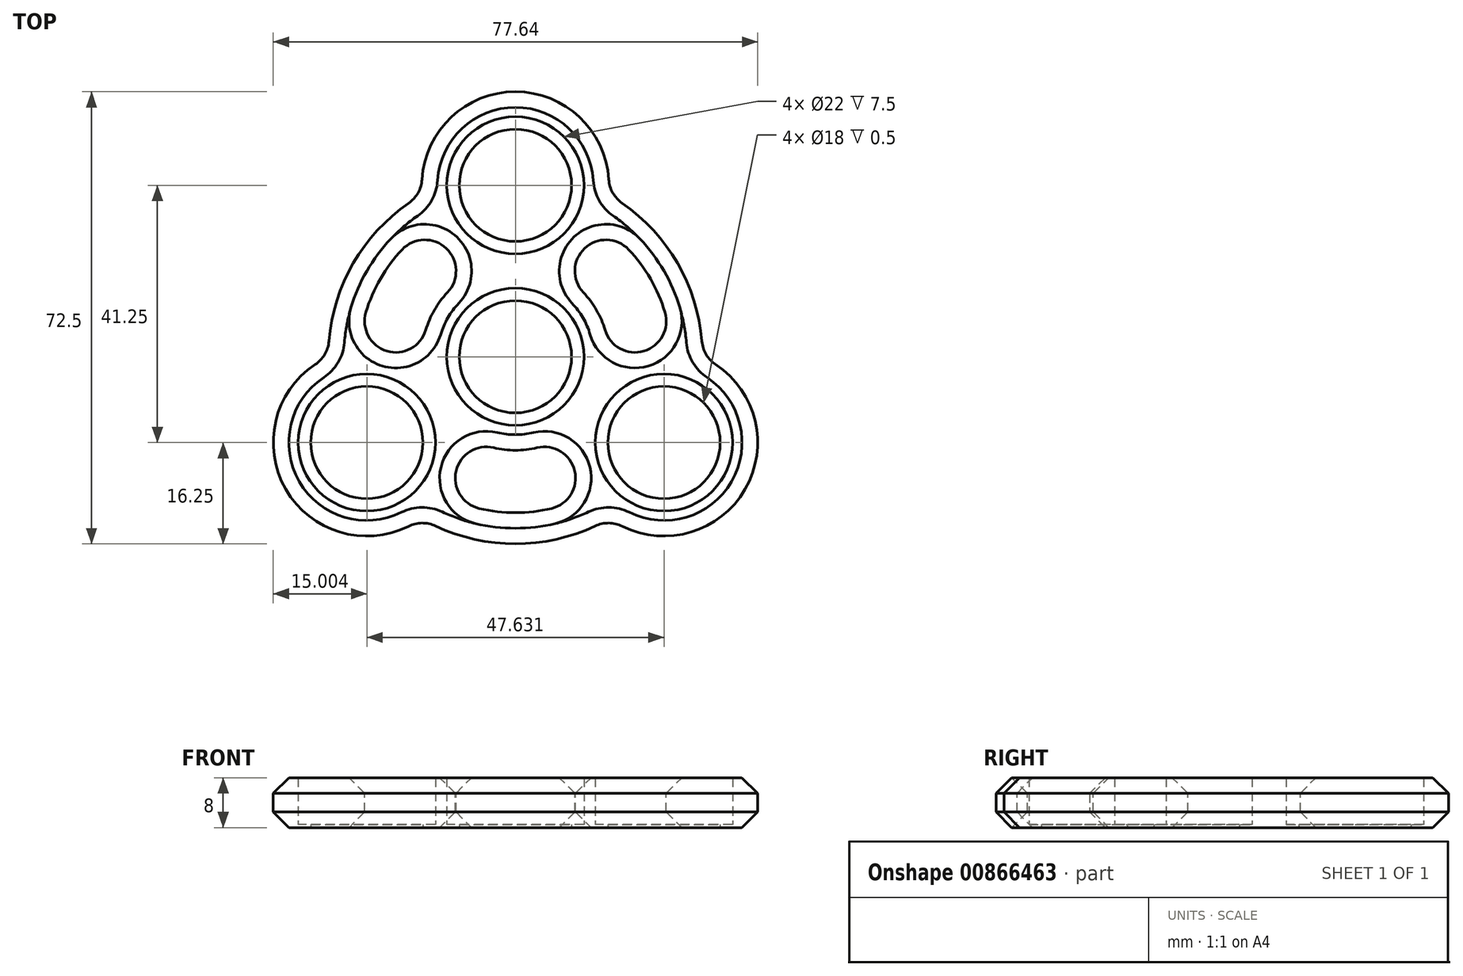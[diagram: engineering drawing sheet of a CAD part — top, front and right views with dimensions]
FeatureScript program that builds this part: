
annotation { "Feature Type Name" : "Feature", "Feature Type Description" : "" }
export const myFeature = defineFeature(function(context is Context, id is Id, definition is map)
    precondition{}
    {
        {
            var Q0;
            Q0=qCreatedBy(makeId("Top.planeOp"),FACE);
            var sketch = newSketch(context, id + "F0", { "sketchPlane" : qUnion([Q0])});
            skCircle(sketch, "E0", {"center": v(0, 0) * mm, "radius": 42.5 * mm, "construction": true});
            skCircle(sketch, "E1", {"center": v(0, 0) * mm, "radius": 15 * mm});
            skCircle(sketch, "E2", {"center": v(0, 0) * mm, "radius": 11 * mm});
            skCircle(sketch, "E3", {"center": v(0, 27.5) * mm, "radius": 15 * mm});
            skCircle(sketch, "E4", {"center": v(0, 27.5) * mm, "radius": 11 * mm});
            skCircle(sketch, "E5.1.0", {"center": v(23.82, -13.75) * mm, "radius": 11 * mm});
            skCircle(sketch, "E5.1.1", {"center": v(23.82, -13.75) * mm, "radius": 15 * mm});
            skCircle(sketch, "E5.2.0", {"center": v(-23.82, -13.75) * mm, "radius": 11 * mm});
            skCircle(sketch, "E5.2.1", {"center": v(-23.82, -13.75) * mm, "radius": 15 * mm});
            skLineSegment(sketch, "E5.anchor1", {"start": v(0, 0) * mm, "end": v(0, 27.5) * mm, "construction": true});
            skLineSegment(sketch, "E5.anchor2", {"start": v(0, 0) * mm, "end": v(-23.82, -13.75) * mm, "construction": true});
            skSolve(sketch);
        }
        {
            var Q0;
            Q0 = qSketchRegion(id + "F0", true);
            extrude(context, id + "F1", {"entities" : qUnion([Q0]), "depth" : 8 * mm, "offsetDistance" : 25 * mm});
        }
        {
            var Q0;
            {var subQ0=sQuery(id+"F0.wireOp",EDGE,"E3");var subQ1=sQuery(id+"F0.wireOp",EDGE,"E1");Q0=makeQuery(id+"F1.opExtrude","SWEPT_EDGE",EDGE,{"disambiguationData":[OSD([subQ1,subQ0]),TDD([makeQuery(id+"F0.imprint","INTERSECT",VERTEX,{"disambiguationData":[OD(0.0)],"derivedFrom":[subQ1,subQ0]})])]});}
            var Q1;
            {var subQ0=sQuery(id+"F0.wireOp",EDGE,"E3");var subQ1=sQuery(id+"F0.wireOp",EDGE,"E1");Q1=makeQuery(id+"F1.opExtrude","SWEPT_EDGE",EDGE,{"disambiguationData":[OSD([subQ1,subQ0]),TDD([makeQuery(id+"F0.imprint","INTERSECT",VERTEX,{"disambiguationData":[OD(1.0)],"derivedFrom":[subQ1,subQ0]})])]});}
            var Q2;
            {var subQ0=sQuery(id+"F0.wireOp",EDGE,"E5.1.1");var subQ1=sQuery(id+"F0.wireOp",EDGE,"E1");Q2=makeQuery(id+"F1.opExtrude","SWEPT_EDGE",EDGE,{"disambiguationData":[OSD([subQ1,subQ0]),TDD([makeQuery(id+"F0.imprint","INTERSECT",VERTEX,{"disambiguationData":[OD(1.0)],"derivedFrom":[subQ1,subQ0]})])]});}
            var Q3;
            {var subQ0=sQuery(id+"F0.wireOp",EDGE,"E5.1.1");var subQ1=sQuery(id+"F0.wireOp",EDGE,"E1");Q3=makeQuery(id+"F1.opExtrude","SWEPT_EDGE",EDGE,{"disambiguationData":[OSD([subQ1,subQ0]),TDD([makeQuery(id+"F0.imprint","INTERSECT",VERTEX,{"disambiguationData":[OD(0.0)],"derivedFrom":[subQ1,subQ0]})])]});}
            var Q4;
            {var subQ0=sQuery(id+"F0.wireOp",EDGE,"E5.2.1");var subQ1=sQuery(id+"F0.wireOp",EDGE,"E1");Q4=makeQuery(id+"F1.opExtrude","SWEPT_EDGE",EDGE,{"disambiguationData":[OSD([subQ1,subQ0]),TDD([makeQuery(id+"F0.imprint","INTERSECT",VERTEX,{"disambiguationData":[OD(1.0)],"derivedFrom":[subQ1,subQ0]})])]});}
            var Q5;
            {var subQ0=sQuery(id+"F0.wireOp",EDGE,"E5.2.1");var subQ1=sQuery(id+"F0.wireOp",EDGE,"E1");Q5=makeQuery(id+"F1.opExtrude","SWEPT_EDGE",EDGE,{"disambiguationData":[OSD([subQ1,subQ0]),TDD([makeQuery(id+"F0.imprint","INTERSECT",VERTEX,{"disambiguationData":[OD(0.0)],"derivedFrom":[subQ1,subQ0]})])]});}
            fillet(context, id + "F2", {"entities" : qUnion([Q0, Q1, Q2, Q3, Q4, Q5]), "radius" : 5 * mm, "tangentPropagation" : true, "allowEdgeOverflow" : false});
        }
        {
            var Q0;
            Q0=makeQuery(id+"F1.opExtrude","CAP_FACE",FACE,{"disambiguationData":[OSD([sQuery(id+"F0.wireOp",EDGE,"E1"),sQuery(id+"F0.wireOp",EDGE,"E2"),sQuery(id+"F0.wireOp",EDGE,"E3"),sQuery(id+"F0.wireOp",EDGE,"E4"),sQuery(id+"F0.wireOp",EDGE,"E5.1.0"),sQuery(id+"F0.wireOp",EDGE,"E5.1.1"),sQuery(id+"F0.wireOp",EDGE,"E5.2.0"),sQuery(id+"F0.wireOp",EDGE,"E5.2.1")])],"isStart":false});
            var sketch = newSketch(context, id + "F3", { "sketchPlane" : qUnion([Q0])});
            skArc(sketch, "E6", {"start": v(-10, 22.91) * mm, "mid": v(-21.65, 12.5) * mm, "end": v(-24.84, -2.8) * mm});
            skArc(sketch, "E7", {"start": v(-11, 27.91) * mm, "mid": v(-25.98, 15) * mm, "end": v(-29.67, -4.44) * mm});
            skArc(sketch, "E8.trimOffspring", {"start": v(-14.84, -20.12) * mm, "mid": v(0, -25) * mm, "end": v(14.84, -20.12) * mm});
            skArc(sketch, "E9.trimOffspring", {"start": v(-18.68, -23.48) * mm, "mid": v(0, -30) * mm, "end": v(18.68, -23.48) * mm});
            skArc(sketch, "E10.trimOffspring", {"start": v(29.67, -4.44) * mm, "mid": v(25.98, 15) * mm, "end": v(11, 27.91) * mm});
            skArc(sketch, "E11.trimOffspring", {"start": v(24.84, -2.8) * mm, "mid": v(21.65, 12.5) * mm, "end": v(10, 22.91) * mm});
            skArc(sketch, "E12", {"start": v(-11, 27.91) * mm, "mid": v(-10.79, 25.36) * mm, "end": v(-10, 22.91) * mm});
            skArc(sketch, "E13", {"start": v(-10, 22.91) * mm, "mid": v(0, 16.5) * mm, "end": v(10, 22.91) * mm, "construction": true});
            skArc(sketch, "E14", {"start": v(11, 27.91) * mm, "mid": v(0, 38.5) * mm, "end": v(-11, 27.91) * mm, "construction": true});
            skArc(sketch, "E15", {"start": v(10, 22.91) * mm, "mid": v(10.79, 25.36) * mm, "end": v(11, 27.91) * mm});
            skArc(sketch, "E16", {"start": v(29.67, -4.44) * mm, "mid": v(27.35, -3.33) * mm, "end": v(24.84, -2.8) * mm});
            skArc(sketch, "E17", {"start": v(-14.84, -20.12) * mm, "mid": v(-14.29, -8.25) * mm, "end": v(-24.84, -2.8) * mm, "construction": true});
            skArc(sketch, "E18", {"start": v(-18.68, -23.48) * mm, "mid": v(-16.56, -22.02) * mm, "end": v(-14.84, -20.12) * mm});
            skArc(sketch, "E19", {"start": v(-24.84, -2.8) * mm, "mid": v(-27.35, -3.33) * mm, "end": v(-29.67, -4.44) * mm});
            skArc(sketch, "E20", {"start": v(-29.67, -4.44) * mm, "mid": v(-33.34, -19.25) * mm, "end": v(-18.68, -23.48) * mm, "construction": true});
            skArc(sketch, "E21", {"start": v(14.84, -20.12) * mm, "mid": v(16.56, -22.02) * mm, "end": v(18.68, -23.48) * mm});
            skArc(sketch, "E22", {"start": v(18.68, -23.48) * mm, "mid": v(31.07, -5.48) * mm, "end": v(14.84, -20.12) * mm, "construction": true});
            skSolve(sketch);
        }
        {
            var Q0;
            Q0 = qSketchRegion(id + "F3", true);
            extrude(context, id + "F4", {"entities" : qUnion([Q0]), "operationType" : NewBodyOperationType.ADD, "oppositeDirection" : true, "depth" : 8 * mm, "offsetDistance" : 25 * mm});
        }
        {
            var Q0;
            Q0=makeQuery(id+"F4.boolean.opBoolean","INTERSECT",EDGE,{"derivedFrom":[makeQuery(id+"F1.opExtrude","SWEPT_FACE",FACE,{"disambiguationData":[OSD([sQuery(id+"F0.wireOp",EDGE,"E3")])]}),makeQuery(id+"F4.opExtrude","SWEPT_FACE",FACE,{"disambiguationData":[OSD([sQuery(id+"F3.wireOp",EDGE,"E6")])]})]});
            var Q1;
            Q1=makeQuery(id+"F4.boolean.opBoolean","INTERSECT",EDGE,{"derivedFrom":[makeQuery(id+"F1.opExtrude","SWEPT_FACE",FACE,{"disambiguationData":[OSD([sQuery(id+"F0.wireOp",EDGE,"E5.2.1")])]}),makeQuery(id+"F4.opExtrude","SWEPT_FACE",FACE,{"disambiguationData":[OSD([sQuery(id+"F3.wireOp",EDGE,"E6")])]})]});
            var Q2;
            Q2=makeQuery(id+"F4.boolean.opBoolean","INTERSECT",EDGE,{"derivedFrom":[makeQuery(id+"F1.opExtrude","SWEPT_FACE",FACE,{"disambiguationData":[OSD([sQuery(id+"F0.wireOp",EDGE,"E3")])]}),makeQuery(id+"F4.opExtrude","SWEPT_FACE",FACE,{"disambiguationData":[OSD([sQuery(id+"F3.wireOp",EDGE,"E11.trimOffspring")])]})]});
            var Q3;
            Q3=makeQuery(id+"F4.boolean.opBoolean","INTERSECT",EDGE,{"derivedFrom":[makeQuery(id+"F1.opExtrude","SWEPT_FACE",FACE,{"disambiguationData":[OSD([sQuery(id+"F0.wireOp",EDGE,"E5.1.1")])]}),makeQuery(id+"F4.opExtrude","SWEPT_FACE",FACE,{"disambiguationData":[OSD([sQuery(id+"F3.wireOp",EDGE,"E11.trimOffspring")])]})]});
            var Q4;
            Q4=makeQuery(id+"F4.boolean.opBoolean","INTERSECT",EDGE,{"derivedFrom":[makeQuery(id+"F1.opExtrude","SWEPT_FACE",FACE,{"disambiguationData":[OSD([sQuery(id+"F0.wireOp",EDGE,"E3")])]}),makeQuery(id+"F4.opExtrude","SWEPT_FACE",FACE,{"disambiguationData":[OSD([sQuery(id+"F3.wireOp",EDGE,"E10.trimOffspring")])]})]});
            var Q5;
            Q5=makeQuery(id+"F4.boolean.opBoolean","INTERSECT",EDGE,{"derivedFrom":[makeQuery(id+"F1.opExtrude","SWEPT_FACE",FACE,{"disambiguationData":[OSD([sQuery(id+"F0.wireOp",EDGE,"E5.1.1")])]}),makeQuery(id+"F4.opExtrude","SWEPT_FACE",FACE,{"disambiguationData":[OSD([sQuery(id+"F3.wireOp",EDGE,"E10.trimOffspring")])]})]});
            var Q6;
            Q6=makeQuery(id+"F4.boolean.opBoolean","INTERSECT",EDGE,{"derivedFrom":[makeQuery(id+"F1.opExtrude","SWEPT_FACE",FACE,{"disambiguationData":[OSD([sQuery(id+"F0.wireOp",EDGE,"E3")])]}),makeQuery(id+"F4.opExtrude","SWEPT_FACE",FACE,{"disambiguationData":[OSD([sQuery(id+"F3.wireOp",EDGE,"E7")])]})]});
            var Q7;
            Q7=makeQuery(id+"F4.boolean.opBoolean","INTERSECT",EDGE,{"derivedFrom":[makeQuery(id+"F1.opExtrude","SWEPT_FACE",FACE,{"disambiguationData":[OSD([sQuery(id+"F0.wireOp",EDGE,"E5.2.1")])]}),makeQuery(id+"F4.opExtrude","SWEPT_FACE",FACE,{"disambiguationData":[OSD([sQuery(id+"F3.wireOp",EDGE,"E9.trimOffspring")])]})]});
            var Q8;
            Q8=makeQuery(id+"F4.boolean.opBoolean","INTERSECT",EDGE,{"derivedFrom":[makeQuery(id+"F1.opExtrude","SWEPT_FACE",FACE,{"disambiguationData":[OSD([sQuery(id+"F0.wireOp",EDGE,"E5.1.1")])]}),makeQuery(id+"F4.opExtrude","SWEPT_FACE",FACE,{"disambiguationData":[OSD([sQuery(id+"F3.wireOp",EDGE,"E9.trimOffspring")])]})]});
            var Q9;
            Q9=makeQuery(id+"F4.boolean.opBoolean","INTERSECT",EDGE,{"derivedFrom":[makeQuery(id+"F1.opExtrude","SWEPT_FACE",FACE,{"disambiguationData":[OSD([sQuery(id+"F0.wireOp",EDGE,"E5.2.1")])]}),makeQuery(id+"F4.opExtrude","SWEPT_FACE",FACE,{"disambiguationData":[OSD([sQuery(id+"F3.wireOp",EDGE,"E7")])]})]});
            var Q10;
            Q10=makeQuery(id+"F4.boolean.opBoolean","INTERSECT",EDGE,{"derivedFrom":[makeQuery(id+"F1.opExtrude","SWEPT_FACE",FACE,{"disambiguationData":[OSD([sQuery(id+"F0.wireOp",EDGE,"E5.1.1")])]}),makeQuery(id+"F4.opExtrude","SWEPT_FACE",FACE,{"disambiguationData":[OSD([sQuery(id+"F3.wireOp",EDGE,"E8.trimOffspring")])]})]});
            var Q11;
            Q11=makeQuery(id+"F4.boolean.opBoolean","INTERSECT",EDGE,{"derivedFrom":[makeQuery(id+"F1.opExtrude","SWEPT_FACE",FACE,{"disambiguationData":[OSD([sQuery(id+"F0.wireOp",EDGE,"E5.2.1")])]}),makeQuery(id+"F4.opExtrude","SWEPT_FACE",FACE,{"disambiguationData":[OSD([sQuery(id+"F3.wireOp",EDGE,"E8.trimOffspring")])]})]});
            fillet(context, id + "F5", {"entities" : qUnion([Q0, Q1, Q2, Q3, Q4, Q5, Q6, Q7, Q8, Q9, Q10, Q11]), "radius" : 5 * mm, "tangentPropagation" : true, "allowEdgeOverflow" : false});
        }
        {
            var Q0;
            Q0=makeQuery(id+"F4.opExtrude","CAP_EDGE",EDGE,{"disambiguationData":[OSD([sQuery(id+"F3.wireOp",EDGE,"E7")])],"isStart":true});
            var Q1;
            {var subQ0=sQuery(id+"F3.wireOp",EDGE,"E7");var subQ1=sQuery(id+"F0.wireOp",EDGE,"E3");Q1=makeQuery(id+"F5.opFillet","BLEND_EDGE",EDGE,{"blendedFrom":[makeQuery(id+"F4.boolean.opBoolean","INTERSECT",EDGE,{"derivedFrom":[makeQuery(id+"F1.opExtrude","SWEPT_FACE",FACE,{"disambiguationData":[OSD([subQ1])]}),makeQuery(id+"F4.opExtrude","SWEPT_FACE",FACE,{"disambiguationData":[OSD([subQ0])]})]}),makeQuery(id+"F4.boolean.opBoolean","MERGE",FACE,{"derivedFrom":[makeQuery(id+"F1.opExtrude","CAP_FACE",FACE,{"disambiguationData":[OSD([sQuery(id+"F0.wireOp",EDGE,"E1"),sQuery(id+"F0.wireOp",EDGE,"E2"),subQ1,sQuery(id+"F0.wireOp",EDGE,"E4"),sQuery(id+"F0.wireOp",EDGE,"E5.1.0"),sQuery(id+"F0.wireOp",EDGE,"E5.1.1"),sQuery(id+"F0.wireOp",EDGE,"E5.2.0"),sQuery(id+"F0.wireOp",EDGE,"E5.2.1")])],"isStart":false}),makeQuery(id+"F4.opExtrude","CAP_FACE",FACE,{"disambiguationData":[OSD([sQuery(id+"F3.wireOp",EDGE,"E6"),subQ0,sQuery(id+"F3.wireOp",EDGE,"E12"),sQuery(id+"F3.wireOp",EDGE,"E19")])],"isStart":true}),makeQuery(id+"F4.opExtrude","CAP_FACE",FACE,{"disambiguationData":[OSD([sQuery(id+"F3.wireOp",EDGE,"E8.trimOffspring"),sQuery(id+"F3.wireOp",EDGE,"E9.trimOffspring"),sQuery(id+"F3.wireOp",EDGE,"E18"),sQuery(id+"F3.wireOp",EDGE,"E21")])],"isStart":true}),makeQuery(id+"F4.opExtrude","CAP_FACE",FACE,{"disambiguationData":[OSD([sQuery(id+"F3.wireOp",EDGE,"E10.trimOffspring"),sQuery(id+"F3.wireOp",EDGE,"E11.trimOffspring"),sQuery(id+"F3.wireOp",EDGE,"E15"),sQuery(id+"F3.wireOp",EDGE,"E16")])],"isStart":true})]})],"blendedInto":[makeQuery(id+"F4.boolean.opBoolean","MERGE",FACE,{"derivedFrom":[makeQuery(id+"F1.opExtrude","CAP_FACE",FACE,{"disambiguationData":[OSD([sQuery(id+"F0.wireOp",EDGE,"E1"),sQuery(id+"F0.wireOp",EDGE,"E2"),subQ1,sQuery(id+"F0.wireOp",EDGE,"E4"),sQuery(id+"F0.wireOp",EDGE,"E5.1.0"),sQuery(id+"F0.wireOp",EDGE,"E5.1.1"),sQuery(id+"F0.wireOp",EDGE,"E5.2.0"),sQuery(id+"F0.wireOp",EDGE,"E5.2.1")])],"isStart":false}),makeQuery(id+"F4.opExtrude","CAP_FACE",FACE,{"disambiguationData":[OSD([sQuery(id+"F3.wireOp",EDGE,"E6"),subQ0,sQuery(id+"F3.wireOp",EDGE,"E12"),sQuery(id+"F3.wireOp",EDGE,"E19")])],"isStart":true}),makeQuery(id+"F4.opExtrude","CAP_FACE",FACE,{"disambiguationData":[OSD([sQuery(id+"F3.wireOp",EDGE,"E8.trimOffspring"),sQuery(id+"F3.wireOp",EDGE,"E9.trimOffspring"),sQuery(id+"F3.wireOp",EDGE,"E18"),sQuery(id+"F3.wireOp",EDGE,"E21")])],"isStart":true}),makeQuery(id+"F4.opExtrude","CAP_FACE",FACE,{"disambiguationData":[OSD([sQuery(id+"F3.wireOp",EDGE,"E10.trimOffspring"),sQuery(id+"F3.wireOp",EDGE,"E11.trimOffspring"),sQuery(id+"F3.wireOp",EDGE,"E15"),sQuery(id+"F3.wireOp",EDGE,"E16")])],"isStart":true})]})]});}
            var Q2;
            Q2=makeQuery(id+"F4.opExtrude","CAP_EDGE",EDGE,{"disambiguationData":[OSD([sQuery(id+"F3.wireOp",EDGE,"E9.trimOffspring")])],"isStart":false});
            var Q3;
            {var subQ0=sQuery(id+"F3.wireOp",EDGE,"E9.trimOffspring");var subQ1=sQuery(id+"F0.wireOp",EDGE,"E5.1.1");Q3=makeQuery(id+"F5.opFillet","BLEND_EDGE",EDGE,{"blendedFrom":[makeQuery(id+"F4.boolean.opBoolean","INTERSECT",EDGE,{"derivedFrom":[makeQuery(id+"F1.opExtrude","SWEPT_FACE",FACE,{"disambiguationData":[OSD([subQ1])]}),makeQuery(id+"F4.opExtrude","SWEPT_FACE",FACE,{"disambiguationData":[OSD([subQ0])]})]}),makeQuery(id+"F4.boolean.opBoolean","MERGE",FACE,{"derivedFrom":[makeQuery(id+"F1.opExtrude","CAP_FACE",FACE,{"disambiguationData":[OSD([sQuery(id+"F0.wireOp",EDGE,"E1"),sQuery(id+"F0.wireOp",EDGE,"E2"),sQuery(id+"F0.wireOp",EDGE,"E3"),sQuery(id+"F0.wireOp",EDGE,"E4"),sQuery(id+"F0.wireOp",EDGE,"E5.1.0"),subQ1,sQuery(id+"F0.wireOp",EDGE,"E5.2.0"),sQuery(id+"F0.wireOp",EDGE,"E5.2.1")])],"isStart":true}),makeQuery(id+"F4.opExtrude","CAP_FACE",FACE,{"disambiguationData":[OSD([sQuery(id+"F3.wireOp",EDGE,"E6"),sQuery(id+"F3.wireOp",EDGE,"E7"),sQuery(id+"F3.wireOp",EDGE,"E12"),sQuery(id+"F3.wireOp",EDGE,"E19")])],"isStart":false}),makeQuery(id+"F4.opExtrude","CAP_FACE",FACE,{"disambiguationData":[OSD([sQuery(id+"F3.wireOp",EDGE,"E8.trimOffspring"),subQ0,sQuery(id+"F3.wireOp",EDGE,"E18"),sQuery(id+"F3.wireOp",EDGE,"E21")])],"isStart":false}),makeQuery(id+"F4.opExtrude","CAP_FACE",FACE,{"disambiguationData":[OSD([sQuery(id+"F3.wireOp",EDGE,"E10.trimOffspring"),sQuery(id+"F3.wireOp",EDGE,"E11.trimOffspring"),sQuery(id+"F3.wireOp",EDGE,"E15"),sQuery(id+"F3.wireOp",EDGE,"E16")])],"isStart":false})]})],"blendedInto":[makeQuery(id+"F4.boolean.opBoolean","MERGE",FACE,{"derivedFrom":[makeQuery(id+"F1.opExtrude","CAP_FACE",FACE,{"disambiguationData":[OSD([sQuery(id+"F0.wireOp",EDGE,"E1"),sQuery(id+"F0.wireOp",EDGE,"E2"),sQuery(id+"F0.wireOp",EDGE,"E3"),sQuery(id+"F0.wireOp",EDGE,"E4"),sQuery(id+"F0.wireOp",EDGE,"E5.1.0"),subQ1,sQuery(id+"F0.wireOp",EDGE,"E5.2.0"),sQuery(id+"F0.wireOp",EDGE,"E5.2.1")])],"isStart":true}),makeQuery(id+"F4.opExtrude","CAP_FACE",FACE,{"disambiguationData":[OSD([sQuery(id+"F3.wireOp",EDGE,"E6"),sQuery(id+"F3.wireOp",EDGE,"E7"),sQuery(id+"F3.wireOp",EDGE,"E12"),sQuery(id+"F3.wireOp",EDGE,"E19")])],"isStart":false}),makeQuery(id+"F4.opExtrude","CAP_FACE",FACE,{"disambiguationData":[OSD([sQuery(id+"F3.wireOp",EDGE,"E8.trimOffspring"),subQ0,sQuery(id+"F3.wireOp",EDGE,"E18"),sQuery(id+"F3.wireOp",EDGE,"E21")])],"isStart":false}),makeQuery(id+"F4.opExtrude","CAP_FACE",FACE,{"disambiguationData":[OSD([sQuery(id+"F3.wireOp",EDGE,"E10.trimOffspring"),sQuery(id+"F3.wireOp",EDGE,"E11.trimOffspring"),sQuery(id+"F3.wireOp",EDGE,"E15"),sQuery(id+"F3.wireOp",EDGE,"E16")])],"isStart":false})]})]});}
            var Q4;
            {var subQ0=sQuery(id+"F3.wireOp",EDGE,"E6");var subQ1=sQuery(id+"F0.wireOp",EDGE,"E3");Q4=makeQuery(id+"F5.opFillet","BLEND_EDGE",EDGE,{"blendedFrom":[makeQuery(id+"F4.boolean.opBoolean","INTERSECT",EDGE,{"derivedFrom":[makeQuery(id+"F1.opExtrude","SWEPT_FACE",FACE,{"disambiguationData":[OSD([subQ1])]}),makeQuery(id+"F4.opExtrude","SWEPT_FACE",FACE,{"disambiguationData":[OSD([subQ0])]})]}),makeQuery(id+"F4.boolean.opBoolean","MERGE",FACE,{"derivedFrom":[makeQuery(id+"F1.opExtrude","CAP_FACE",FACE,{"disambiguationData":[OSD([sQuery(id+"F0.wireOp",EDGE,"E1"),sQuery(id+"F0.wireOp",EDGE,"E2"),subQ1,sQuery(id+"F0.wireOp",EDGE,"E4"),sQuery(id+"F0.wireOp",EDGE,"E5.1.0"),sQuery(id+"F0.wireOp",EDGE,"E5.1.1"),sQuery(id+"F0.wireOp",EDGE,"E5.2.0"),sQuery(id+"F0.wireOp",EDGE,"E5.2.1")])],"isStart":false}),makeQuery(id+"F4.opExtrude","CAP_FACE",FACE,{"disambiguationData":[OSD([subQ0,sQuery(id+"F3.wireOp",EDGE,"E7"),sQuery(id+"F3.wireOp",EDGE,"E12"),sQuery(id+"F3.wireOp",EDGE,"E19")])],"isStart":true}),makeQuery(id+"F4.opExtrude","CAP_FACE",FACE,{"disambiguationData":[OSD([sQuery(id+"F3.wireOp",EDGE,"E8.trimOffspring"),sQuery(id+"F3.wireOp",EDGE,"E9.trimOffspring"),sQuery(id+"F3.wireOp",EDGE,"E18"),sQuery(id+"F3.wireOp",EDGE,"E21")])],"isStart":true}),makeQuery(id+"F4.opExtrude","CAP_FACE",FACE,{"disambiguationData":[OSD([sQuery(id+"F3.wireOp",EDGE,"E10.trimOffspring"),sQuery(id+"F3.wireOp",EDGE,"E11.trimOffspring"),sQuery(id+"F3.wireOp",EDGE,"E15"),sQuery(id+"F3.wireOp",EDGE,"E16")])],"isStart":true})]})],"blendedInto":[makeQuery(id+"F4.boolean.opBoolean","MERGE",FACE,{"derivedFrom":[makeQuery(id+"F1.opExtrude","CAP_FACE",FACE,{"disambiguationData":[OSD([sQuery(id+"F0.wireOp",EDGE,"E1"),sQuery(id+"F0.wireOp",EDGE,"E2"),subQ1,sQuery(id+"F0.wireOp",EDGE,"E4"),sQuery(id+"F0.wireOp",EDGE,"E5.1.0"),sQuery(id+"F0.wireOp",EDGE,"E5.1.1"),sQuery(id+"F0.wireOp",EDGE,"E5.2.0"),sQuery(id+"F0.wireOp",EDGE,"E5.2.1")])],"isStart":false}),makeQuery(id+"F4.opExtrude","CAP_FACE",FACE,{"disambiguationData":[OSD([subQ0,sQuery(id+"F3.wireOp",EDGE,"E7"),sQuery(id+"F3.wireOp",EDGE,"E12"),sQuery(id+"F3.wireOp",EDGE,"E19")])],"isStart":true}),makeQuery(id+"F4.opExtrude","CAP_FACE",FACE,{"disambiguationData":[OSD([sQuery(id+"F3.wireOp",EDGE,"E8.trimOffspring"),sQuery(id+"F3.wireOp",EDGE,"E9.trimOffspring"),sQuery(id+"F3.wireOp",EDGE,"E18"),sQuery(id+"F3.wireOp",EDGE,"E21")])],"isStart":true}),makeQuery(id+"F4.opExtrude","CAP_FACE",FACE,{"disambiguationData":[OSD([sQuery(id+"F3.wireOp",EDGE,"E10.trimOffspring"),sQuery(id+"F3.wireOp",EDGE,"E11.trimOffspring"),sQuery(id+"F3.wireOp",EDGE,"E15"),sQuery(id+"F3.wireOp",EDGE,"E16")])],"isStart":true})]})]});}
            var Q5;
            Q5=makeQuery(id+"F4.opExtrude","CAP_EDGE",EDGE,{"disambiguationData":[OSD([sQuery(id+"F3.wireOp",EDGE,"E11.trimOffspring")])],"isStart":true});
            var Q6;
            {var subQ0=sQuery(id+"F0.wireOp",EDGE,"E5.1.1");var subQ1=sQuery(id+"F0.wireOp",EDGE,"E1");Q6=makeQuery(id+"F2.opFillet","BLEND_EDGE",EDGE,{"blendedFrom":[makeQuery(id+"F1.opExtrude","SWEPT_EDGE",EDGE,{"disambiguationData":[OSD([subQ1,subQ0]),TDD([makeQuery(id+"F0.imprint","INTERSECT",VERTEX,{"disambiguationData":[OD(0.0)],"derivedFrom":[subQ1,subQ0]})])]}),makeQuery(id+"F1.opExtrude","CAP_FACE",FACE,{"disambiguationData":[OSD([subQ1,sQuery(id+"F0.wireOp",EDGE,"E2"),sQuery(id+"F0.wireOp",EDGE,"E3"),sQuery(id+"F0.wireOp",EDGE,"E4"),sQuery(id+"F0.wireOp",EDGE,"E5.1.0"),subQ0,sQuery(id+"F0.wireOp",EDGE,"E5.2.0"),sQuery(id+"F0.wireOp",EDGE,"E5.2.1")])],"isStart":false})],"blendedInto":[makeQuery(id+"F1.opExtrude","CAP_FACE",FACE,{"disambiguationData":[OSD([subQ1,sQuery(id+"F0.wireOp",EDGE,"E2"),sQuery(id+"F0.wireOp",EDGE,"E3"),sQuery(id+"F0.wireOp",EDGE,"E4"),sQuery(id+"F0.wireOp",EDGE,"E5.1.0"),subQ0,sQuery(id+"F0.wireOp",EDGE,"E5.2.0"),sQuery(id+"F0.wireOp",EDGE,"E5.2.1")])],"isStart":false})]});}
            var Q7;
            {var subQ0=sQuery(id+"F3.wireOp",EDGE,"E11.trimOffspring");var subQ1=sQuery(id+"F0.wireOp",EDGE,"E5.1.1");Q7=makeQuery(id+"F5.opFillet","BLEND_EDGE",EDGE,{"blendedFrom":[makeQuery(id+"F4.boolean.opBoolean","INTERSECT",EDGE,{"derivedFrom":[makeQuery(id+"F1.opExtrude","SWEPT_FACE",FACE,{"disambiguationData":[OSD([subQ1])]}),makeQuery(id+"F4.opExtrude","SWEPT_FACE",FACE,{"disambiguationData":[OSD([subQ0])]})]}),makeQuery(id+"F4.boolean.opBoolean","MERGE",FACE,{"derivedFrom":[makeQuery(id+"F1.opExtrude","CAP_FACE",FACE,{"disambiguationData":[OSD([sQuery(id+"F0.wireOp",EDGE,"E1"),sQuery(id+"F0.wireOp",EDGE,"E2"),sQuery(id+"F0.wireOp",EDGE,"E3"),sQuery(id+"F0.wireOp",EDGE,"E4"),sQuery(id+"F0.wireOp",EDGE,"E5.1.0"),subQ1,sQuery(id+"F0.wireOp",EDGE,"E5.2.0"),sQuery(id+"F0.wireOp",EDGE,"E5.2.1")])],"isStart":true}),makeQuery(id+"F4.opExtrude","CAP_FACE",FACE,{"disambiguationData":[OSD([sQuery(id+"F3.wireOp",EDGE,"E6"),sQuery(id+"F3.wireOp",EDGE,"E7"),sQuery(id+"F3.wireOp",EDGE,"E12"),sQuery(id+"F3.wireOp",EDGE,"E19")])],"isStart":false}),makeQuery(id+"F4.opExtrude","CAP_FACE",FACE,{"disambiguationData":[OSD([sQuery(id+"F3.wireOp",EDGE,"E8.trimOffspring"),sQuery(id+"F3.wireOp",EDGE,"E9.trimOffspring"),sQuery(id+"F3.wireOp",EDGE,"E18"),sQuery(id+"F3.wireOp",EDGE,"E21")])],"isStart":false}),makeQuery(id+"F4.opExtrude","CAP_FACE",FACE,{"disambiguationData":[OSD([sQuery(id+"F3.wireOp",EDGE,"E10.trimOffspring"),subQ0,sQuery(id+"F3.wireOp",EDGE,"E15"),sQuery(id+"F3.wireOp",EDGE,"E16")])],"isStart":false})]})],"blendedInto":[makeQuery(id+"F4.boolean.opBoolean","MERGE",FACE,{"derivedFrom":[makeQuery(id+"F1.opExtrude","CAP_FACE",FACE,{"disambiguationData":[OSD([sQuery(id+"F0.wireOp",EDGE,"E1"),sQuery(id+"F0.wireOp",EDGE,"E2"),sQuery(id+"F0.wireOp",EDGE,"E3"),sQuery(id+"F0.wireOp",EDGE,"E4"),sQuery(id+"F0.wireOp",EDGE,"E5.1.0"),subQ1,sQuery(id+"F0.wireOp",EDGE,"E5.2.0"),sQuery(id+"F0.wireOp",EDGE,"E5.2.1")])],"isStart":true}),makeQuery(id+"F4.opExtrude","CAP_FACE",FACE,{"disambiguationData":[OSD([sQuery(id+"F3.wireOp",EDGE,"E6"),sQuery(id+"F3.wireOp",EDGE,"E7"),sQuery(id+"F3.wireOp",EDGE,"E12"),sQuery(id+"F3.wireOp",EDGE,"E19")])],"isStart":false}),makeQuery(id+"F4.opExtrude","CAP_FACE",FACE,{"disambiguationData":[OSD([sQuery(id+"F3.wireOp",EDGE,"E8.trimOffspring"),sQuery(id+"F3.wireOp",EDGE,"E9.trimOffspring"),sQuery(id+"F3.wireOp",EDGE,"E18"),sQuery(id+"F3.wireOp",EDGE,"E21")])],"isStart":false}),makeQuery(id+"F4.opExtrude","CAP_FACE",FACE,{"disambiguationData":[OSD([sQuery(id+"F3.wireOp",EDGE,"E10.trimOffspring"),subQ0,sQuery(id+"F3.wireOp",EDGE,"E15"),sQuery(id+"F3.wireOp",EDGE,"E16")])],"isStart":false})]})]});}
            var Q8;
            {var subQ0=sQuery(id+"F0.wireOp",EDGE,"E5.1.1");var subQ1=sQuery(id+"F0.wireOp",EDGE,"E1");Q8=makeQuery(id+"F2.opFillet","BLEND_EDGE",EDGE,{"blendedFrom":[makeQuery(id+"F1.opExtrude","SWEPT_EDGE",EDGE,{"disambiguationData":[OSD([subQ1,subQ0]),TDD([makeQuery(id+"F0.imprint","INTERSECT",VERTEX,{"disambiguationData":[OD(0.0)],"derivedFrom":[subQ1,subQ0]})])]}),makeQuery(id+"F1.opExtrude","CAP_FACE",FACE,{"disambiguationData":[OSD([subQ1,sQuery(id+"F0.wireOp",EDGE,"E2"),sQuery(id+"F0.wireOp",EDGE,"E3"),sQuery(id+"F0.wireOp",EDGE,"E4"),sQuery(id+"F0.wireOp",EDGE,"E5.1.0"),subQ0,sQuery(id+"F0.wireOp",EDGE,"E5.2.0"),sQuery(id+"F0.wireOp",EDGE,"E5.2.1")])],"isStart":true})],"blendedInto":[makeQuery(id+"F1.opExtrude","CAP_FACE",FACE,{"disambiguationData":[OSD([subQ1,sQuery(id+"F0.wireOp",EDGE,"E2"),sQuery(id+"F0.wireOp",EDGE,"E3"),sQuery(id+"F0.wireOp",EDGE,"E4"),sQuery(id+"F0.wireOp",EDGE,"E5.1.0"),subQ0,sQuery(id+"F0.wireOp",EDGE,"E5.2.0"),sQuery(id+"F0.wireOp",EDGE,"E5.2.1")])],"isStart":true})]});}
            var Q9;
            {var subQ0=sQuery(id+"F0.wireOp",EDGE,"E1");Q9=makeQuery(id+"F1.opExtrude","CAP_EDGE",EDGE,{"disambiguationData":[OSD([subQ0]),TDD([makeQuery(id+"F0.imprint","IMPRINT",EDGE,{"disambiguationData":[TD([[makeQuery(id+"F0.imprint","INTERSECT",VERTEX,{"disambiguationData":[OD(0.0)],"derivedFrom":[subQ0,sQuery(id+"F0.wireOp",EDGE,"E3")]}),-1.0]])],"derivedFrom":subQ0})])],"isStart":true});}
            chamfer(context, id + "F6", {"entities" : qUnion([Q0, Q1, Q2, Q3, Q4, Q5, Q6, Q7, Q8, Q9]), "width" : 2.5 * mm, "tangentPropagation" : true});
        }
        {
            var Q0;
            Q0=makeQuery(id+"F4.boolean.opBoolean","MERGE",FACE,{"derivedFrom":[makeQuery(id+"F1.opExtrude","CAP_FACE",FACE,{"disambiguationData":[OSD([sQuery(id+"F0.wireOp",EDGE,"E1"),sQuery(id+"F0.wireOp",EDGE,"E2"),sQuery(id+"F0.wireOp",EDGE,"E3"),sQuery(id+"F0.wireOp",EDGE,"E4"),sQuery(id+"F0.wireOp",EDGE,"E5.1.0"),sQuery(id+"F0.wireOp",EDGE,"E5.1.1"),sQuery(id+"F0.wireOp",EDGE,"E5.2.0"),sQuery(id+"F0.wireOp",EDGE,"E5.2.1")])],"isStart":true}),makeQuery(id+"F4.opExtrude","CAP_FACE",FACE,{"disambiguationData":[OSD([sQuery(id+"F3.wireOp",EDGE,"E6"),sQuery(id+"F3.wireOp",EDGE,"E7"),sQuery(id+"F3.wireOp",EDGE,"E12"),sQuery(id+"F3.wireOp",EDGE,"E19")])],"isStart":false}),makeQuery(id+"F4.opExtrude","CAP_FACE",FACE,{"disambiguationData":[OSD([sQuery(id+"F3.wireOp",EDGE,"E8.trimOffspring"),sQuery(id+"F3.wireOp",EDGE,"E9.trimOffspring"),sQuery(id+"F3.wireOp",EDGE,"E18"),sQuery(id+"F3.wireOp",EDGE,"E21")])],"isStart":false}),makeQuery(id+"F4.opExtrude","CAP_FACE",FACE,{"disambiguationData":[OSD([sQuery(id+"F3.wireOp",EDGE,"E10.trimOffspring"),sQuery(id+"F3.wireOp",EDGE,"E11.trimOffspring"),sQuery(id+"F3.wireOp",EDGE,"E15"),sQuery(id+"F3.wireOp",EDGE,"E16")])],"isStart":false})]});
            var sketch = newSketch(context, id + "F7", { "sketchPlane" : qUnion([Q0])});
            skCircle(sketch, "E23.0", {"center": v(-23.82, 13.75) * mm, "radius": 11 * mm});
            skCircle(sketch, "E24.0", {"center": v(23.82, 13.75) * mm, "radius": 11 * mm});
            skCircle(sketch, "E25.0", {"center": v(0, 0) * mm, "radius": 11 * mm});
            skCircle(sketch, "E26.0", {"center": v(0, -27.5) * mm, "radius": 11 * mm});
            skCircle(sketch, "E27", {"center": v(-23.82, 13.75) * mm, "radius": 9 * mm});
            skCircle(sketch, "E28", {"center": v(0, 0) * mm, "radius": 9 * mm});
            skCircle(sketch, "E29", {"center": v(23.82, 13.75) * mm, "radius": 9 * mm});
            skCircle(sketch, "E30", {"center": v(0, -27.5) * mm, "radius": 9 * mm});
            skSolve(sketch);
        }
        {
            var Q0;
            Q0 = qSketchRegion(id + "F7", true);
            extrude(context, id + "F8", {"entities" : qUnion([Q0]), "operationType" : NewBodyOperationType.ADD, "oppositeDirection" : true, "depth" : 0.5 * mm, "offsetDistance" : 25 * mm});
        }
    });
